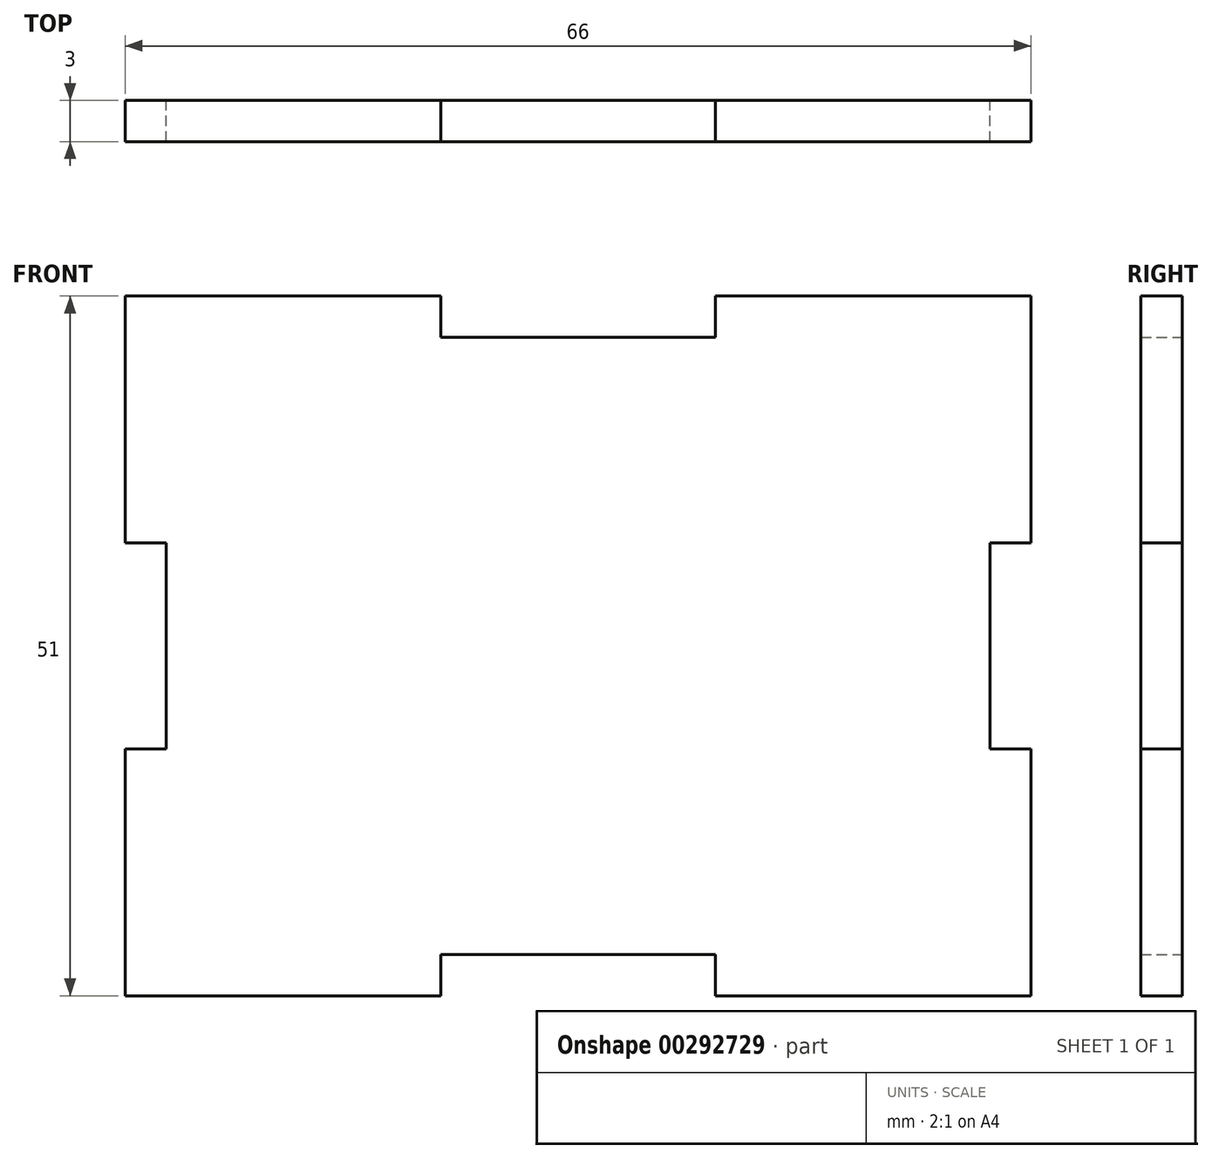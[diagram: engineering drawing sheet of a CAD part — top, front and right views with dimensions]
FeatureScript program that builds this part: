
annotation { "Feature Type Name" : "Feature", "Feature Type Description" : "" }
export const myFeature = defineFeature(function(context is Context, id is Id, definition is map)
    precondition{}
    {
        {
            var Q0;
            Q0=qCreatedBy(makeId("Front.planeOp"),FACE);
            var sketch = newSketch(context, id + "F0", { "sketchPlane" : qUnion([Q0])});
            skLineSegment(sketch, "E0", {"start": v(0, 22.5) * mm, "end": v(-10, 22.5) * mm});
            skLineSegment(sketch, "E1", {"start": v(-10, 22.5) * mm, "end": v(-10, 25.5) * mm});
            skLineSegment(sketch, "E2", {"start": v(-10, 25.5) * mm, "end": v(-33, 25.5) * mm});
            skLineSegment(sketch, "E3", {"start": v(-33, 25.5) * mm, "end": v(-33, 7.5) * mm});
            skLineSegment(sketch, "E4", {"start": v(-33, 7.5) * mm, "end": v(-30, 7.5) * mm});
            skLineSegment(sketch, "E5", {"start": v(-30, 7.5) * mm, "end": v(-30, 0) * mm});
            skLineSegment(sketch, "E6.MirrorCS", {"start": v(33, 7.5) * mm, "end": v(30, 7.5) * mm});
            skLineSegment(sketch, "E7.MirrorCS", {"start": v(10, 22.5) * mm, "end": v(10, 25.5) * mm});
            skLineSegment(sketch, "E8.MirrorCS", {"start": v(30, 7.5) * mm, "end": v(30, 0) * mm});
            skLineSegment(sketch, "E9.MirrorCS", {"start": v(0, 22.5) * mm, "end": v(10, 22.5) * mm});
            skLineSegment(sketch, "E10.MirrorCS", {"start": v(33, 25.5) * mm, "end": v(33, 7.5) * mm});
            skLineSegment(sketch, "E11.MirrorCS", {"start": v(10, 25.5) * mm, "end": v(33, 25.5) * mm});
            skLineSegment(sketch, "E12.MirrorCS", {"start": v(10, -22.5) * mm, "end": v(10, -25.5) * mm});
            skLineSegment(sketch, "E13.MirrorCS", {"start": v(33, -7.5) * mm, "end": v(30, -7.5) * mm});
            skLineSegment(sketch, "E14.MirrorCS", {"start": v(-10, -22.5) * mm, "end": v(-10, -25.5) * mm});
            skLineSegment(sketch, "E15.MirrorCS", {"start": v(-33, -7.5) * mm, "end": v(-30, -7.5) * mm});
            skLineSegment(sketch, "E16.MirrorCS", {"start": v(10, -25.5) * mm, "end": v(33, -25.5) * mm});
            skLineSegment(sketch, "E17.MirrorCS", {"start": v(33, -25.5) * mm, "end": v(33, -7.5) * mm});
            skLineSegment(sketch, "E18.MirrorCS", {"start": v(0, -22.5) * mm, "end": v(10, -22.5) * mm});
            skLineSegment(sketch, "E19.MirrorCS", {"start": v(30, -7.5) * mm, "end": v(30, 0) * mm});
            skLineSegment(sketch, "E20.MirrorCS", {"start": v(-10, -25.5) * mm, "end": v(-33, -25.5) * mm});
            skLineSegment(sketch, "E21.MirrorCS", {"start": v(0, -22.5) * mm, "end": v(-10, -22.5) * mm});
            skLineSegment(sketch, "E22.MirrorCS", {"start": v(-30, -7.5) * mm, "end": v(-30, 0) * mm});
            skLineSegment(sketch, "E23.MirrorCS", {"start": v(-33, -25.5) * mm, "end": v(-33, -7.5) * mm});
            skSolve(sketch);
        }
        {
            var Q0;
            Q0 = qSketchRegion(id + "F0", true);
            extrude(context, id + "F1", {"entities" : qUnion([Q0]), "depth" : 3 * mm});
        }
    });
